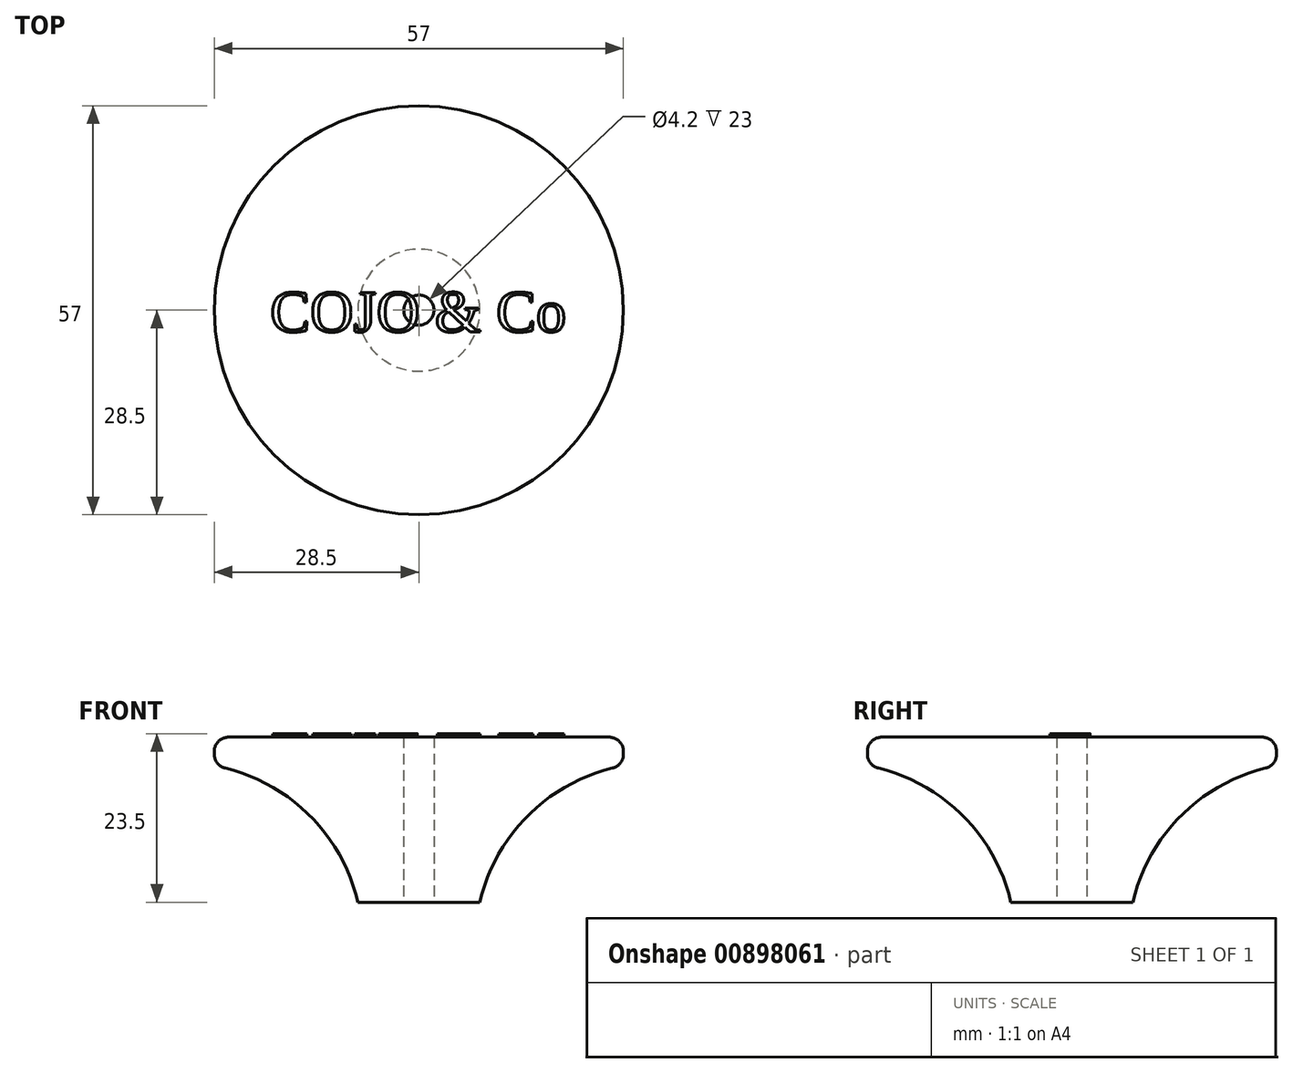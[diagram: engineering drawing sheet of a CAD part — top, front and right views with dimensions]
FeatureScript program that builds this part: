
annotation { "Feature Type Name" : "Feature", "Feature Type Description" : "" }
export const myFeature = defineFeature(function(context is Context, id is Id, definition is map)
    precondition{}
    {
        {
            var Q0;
            Q0=qCreatedBy(makeId("Front.planeOp"),FACE);
            var sketch = newSketch(context, id + "F0", { "sketchPlane" : qUnion([Q0])});
            skLineSegment(sketch, "E0", {"start": v(0, 0) * mm, "end": v(0, 23) * mm});
            skLineSegment(sketch, "E1", {"start": v(0, 23) * mm, "end": v(-28.5, 23) * mm});
            skLineSegment(sketch, "E2", {"start": v(-28.5, 23) * mm, "end": v(-28.5, 19) * mm});
            skArc(sketch, "E3", {"start": v(-8.5, 0) * mm, "mid": v(-15.64, 12.5) * mm, "end": v(-28.5, 19) * mm});
            skLineSegment(sketch, "E4", {"start": v(-8.5, 0) * mm, "end": v(0, 0) * mm});
            skSolve(sketch);
        }
        {
            var Q0;
            Q0 = qSketchRegion(id + "F0", true);
            var Q1;
            Q1=sQuery(id+"F0.wireOp",EDGE,"E0");
            revolve(context, id + "F1", {"surfaceOperationType" : NewSurfaceOperationType.NEW, "entities" : qUnion([Q0]), "axis" : qUnion([Q1]), "revolveType" : RevolveType.FULL});
        }
        {
            var Q0;
            Q0=makeQuery(id+"F1.opRevolve","SWEPT_EDGE",EDGE,{"disambiguationData":[OSD([sQuery(id+"F0.wireOp",EDGE,"E1"),sQuery(id+"F0.wireOp",EDGE,"E2")])]});
            var Q1;
            Q1=makeQuery(id+"F1.opRevolve","SWEPT_EDGE",EDGE,{"disambiguationData":[OSD([sQuery(id+"F0.wireOp",EDGE,"E2"),sQuery(id+"F0.wireOp",EDGE,"E3")])]});
            fillet(context, id + "F2", {"entities" : qUnion([Q0, Q1]), "radius" : 2 * mm, "tangentPropagation" : true, "allowEdgeOverflow" : false});
        }
        {
            var Q0;
            Q0=makeQuery(id+"F1.opRevolve","SWEPT_FACE",FACE,{"disambiguationData":[OSD([sQuery(id+"F0.wireOp",EDGE,"E4")])]});
            var sketch = newSketch(context, id + "F3", { "sketchPlane" : qUnion([Q0])});
            skCircle(sketch, "E5", {"center": v(0, 0) * mm, "radius": 2.1 * mm});
            skSolve(sketch);
        }
        {
            var Q0;
            Q0 = qSketchRegion(id + "F3", true);
            extrude(context, id + "F4", {"entities" : qUnion([Q0]), "operationType" : NewBodyOperationType.REMOVE, "endBound" : BoundingType.UP_TO_NEXT, "oppositeDirection" : true, "depth" : 25 * mm, "offsetDistance" : 25 * mm});
        }
        {
            var Q0;
            Q0=makeQuery(id+"F1.opRevolve","SWEPT_FACE",FACE,{"disambiguationData":[OSD([sQuery(id+"F0.wireOp",EDGE,"E4")])]});
            var sketch = newSketch(context, id + "F5", { "sketchPlane" : qUnion([Q0])});
            skCircle(sketch, "E6", {"center": v(0, 0) * mm, "radius": 4 * mm});
            skCircle(sketch, "E7.0", {"center": v(0, 0) * mm, "radius": 2.1 * mm});
            skSolve(sketch);
        }
        {
            var Q0;
            Q0 = qSketchRegion(id + "F5", true);
            extrude(context, id + "F6", {"entities" : qUnion([Q0]), "operationType" : NewBodyOperationType.ADD, "oppositeDirection" : true, "depth" : 6 * mm, "offsetDistance" : 25 * mm});
        }
        {
            var Q0;
            Q0=makeQuery(id+"F1.opRevolve","SWEPT_FACE",FACE,{"disambiguationData":[OSD([sQuery(id+"F0.wireOp",EDGE,"E1")])]});
            var sketch = newSketch(context, id + "F7", { "sketchPlane" : qUnion([Q0])});
            skLineSegment(sketch, "E8", {"start": v(-26.33, -3) * mm, "end": v(26.33, -3) * mm, "construction": true});
            skText(sketch, "E9", { "text": "COJO & Co", "fontName": "Tinos-Regular.ttf"});
            const initialGuessF7  = {"E9": [-0.0207, -0.003, 1, 0, 0.006]};
            skSetInitialGuess(sketch, initialGuessF7);
            skSolve(sketch);
        }
        {
            var Q0;
            Q0 = qSketchRegion(id + "F7", true);
            extrude(context, id + "F8", {"entities" : qUnion([Q0]), "operationType" : NewBodyOperationType.ADD, "depth" : .5 * mm, "offsetDistance" : 25 * mm});
        }
    });
